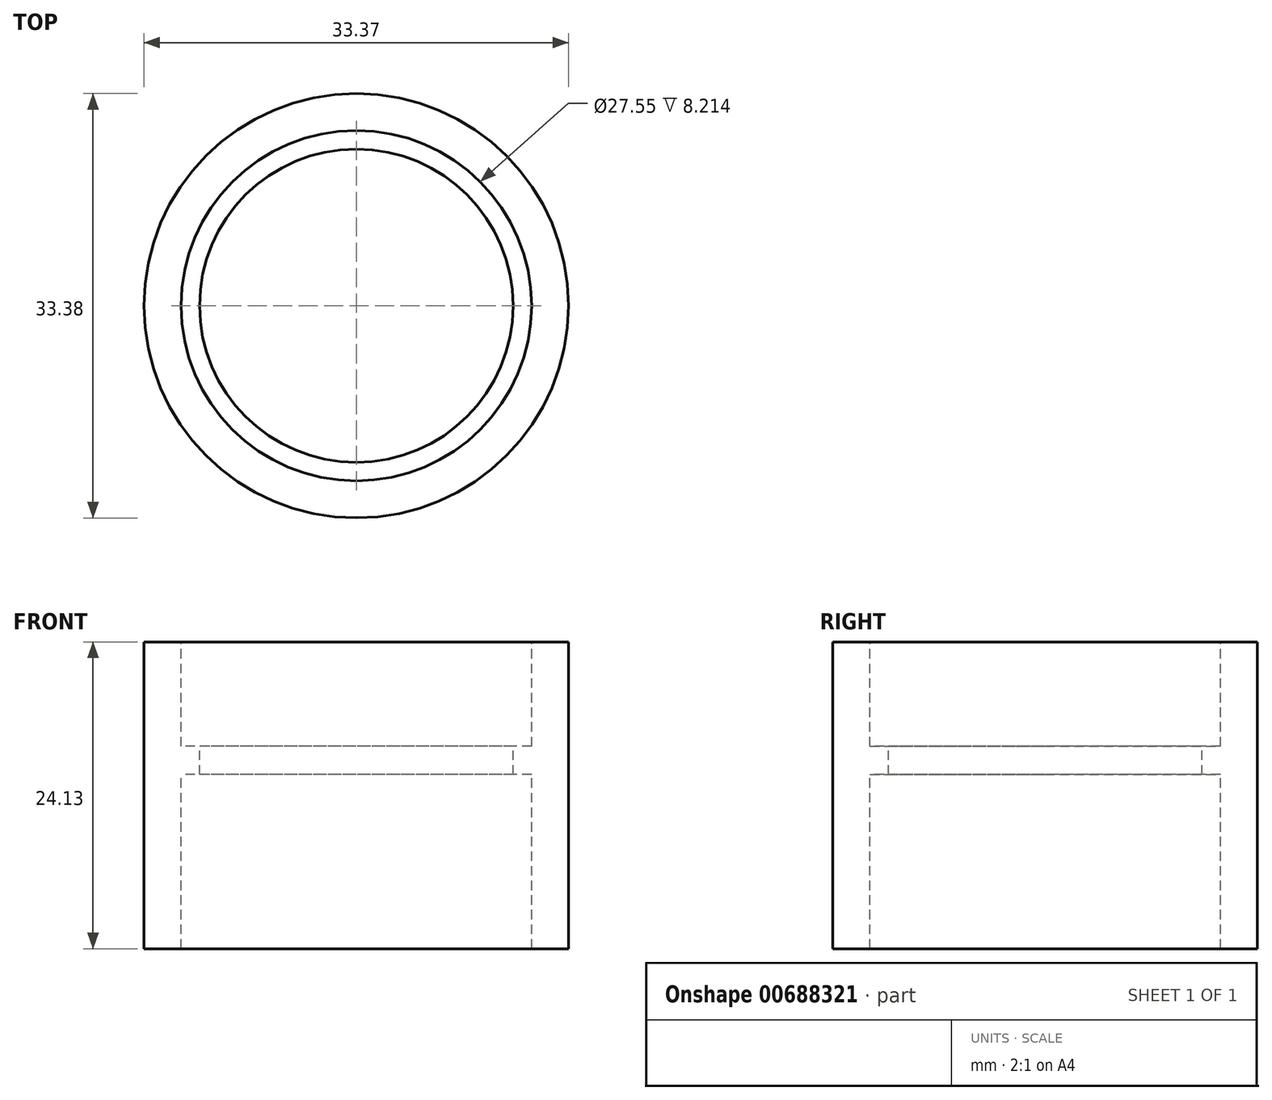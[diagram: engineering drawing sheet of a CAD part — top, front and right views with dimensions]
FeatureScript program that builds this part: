
annotation { "Feature Type Name" : "Feature", "Feature Type Description" : "" }
export const myFeature = defineFeature(function(context is Context, id is Id, definition is map)
    precondition{}
    {
        {
            var Q0;
            Q0=qCreatedBy(makeId("Front.planeOp"),FACE);
            var sketch = newSketch(context, id + "F0", { "sketchPlane" : qUnion([Q0])});
            skLineSegment(sketch, "E0", {"start": v(-39.47, 44.24) * mm, "end": v(-39.47, 20.11) * mm});
            skLineSegment(sketch, "E1", {"start": v(-39.47, 20.11) * mm, "end": v(-36.56, 20.11) * mm});
            skLineSegment(sketch, "E2", {"start": v(-36.56, 20.11) * mm, "end": v(-36.56, 33.8) * mm});
            skLineSegment(sketch, "E3", {"start": v(-36.56, 33.8) * mm, "end": v(-35.1, 33.8) * mm});
            skLineSegment(sketch, "E4", {"start": v(-35.1, 33.8) * mm, "end": v(-35.1, 36.03) * mm});
            skLineSegment(sketch, "E5", {"start": v(-35.1, 36.03) * mm, "end": v(-36.56, 36.03) * mm});
            skLineSegment(sketch, "E6", {"start": v(-36.56, 36.03) * mm, "end": v(-36.56, 44.24) * mm});
            skLineSegment(sketch, "E7", {"start": v(-36.56, 44.24) * mm, "end": v(-39.47, 44.24) * mm});
            skLineSegment(sketch, "E8", {"start": v(-22.78, 44.24) * mm, "end": v(-22.78, 20.11) * mm});
            skSolve(sketch);
        }
        {
            var Q0;
            Q0=makeQuery(id+"F0.imprint","IMPRINT",FACE,{"disambiguationData":[TD([[makeQuery(id+"F0.imprint","IMPRINT",EDGE,{"derivedFrom":sQuery(id+"F0.wireOp",EDGE,"E0")}),1.0]])]});
            var Q1;
            Q1=sQuery(id+"F0.wireOp",EDGE,"E8");
            revolve(context, id + "F1", {"surfaceOperationType" : NewSurfaceOperationType.NEW, "entities" : qUnion([Q0]), "axis" : qUnion([Q1]), "revolveType" : RevolveType.FULL});
        }
    });
